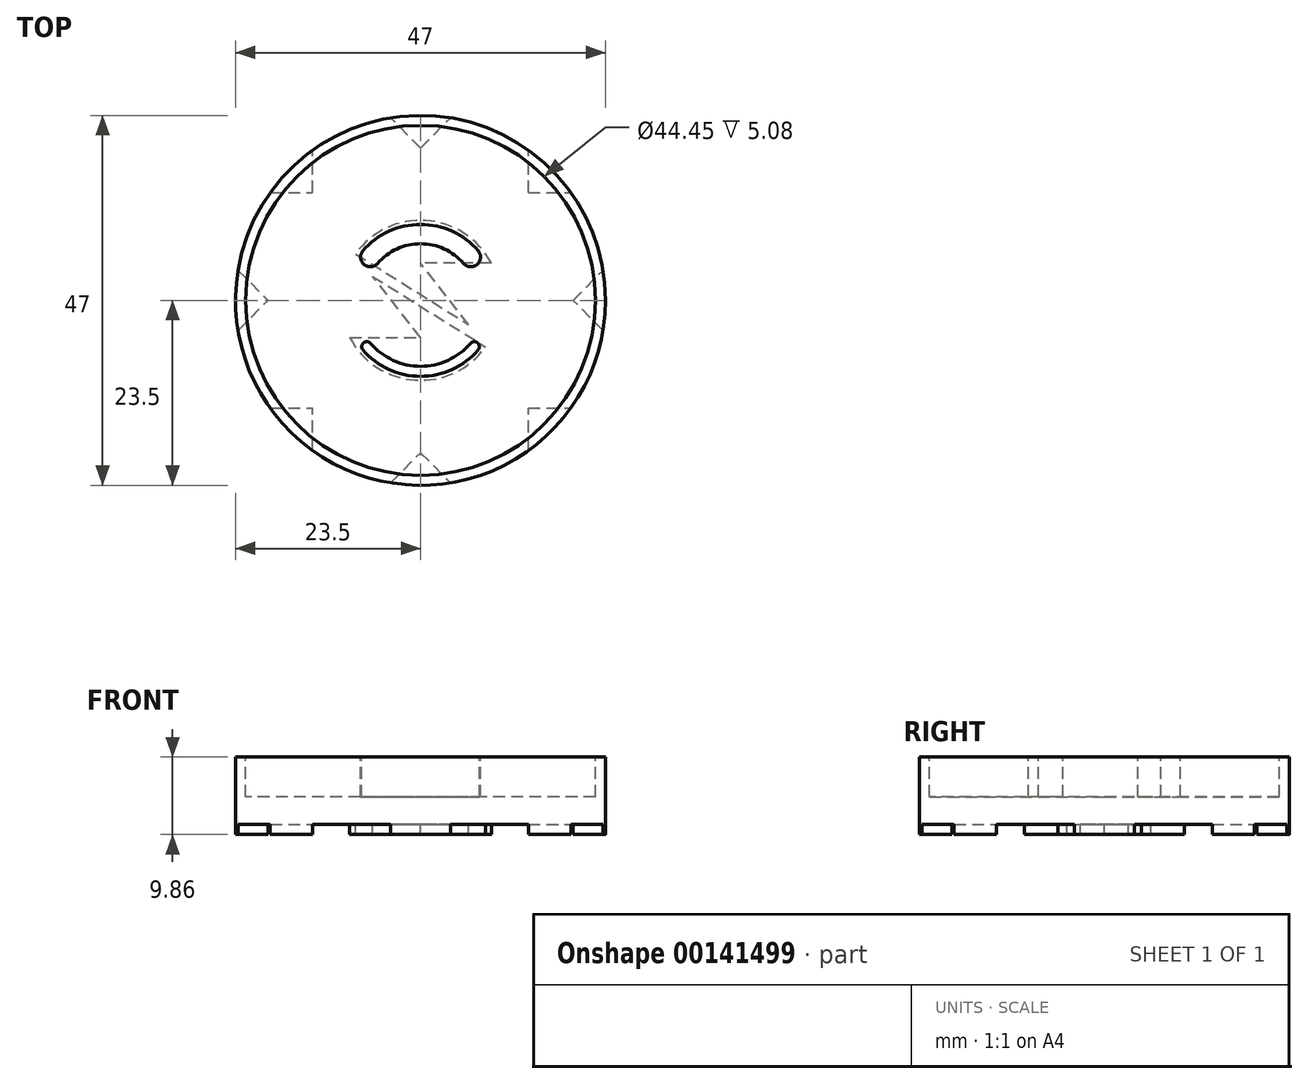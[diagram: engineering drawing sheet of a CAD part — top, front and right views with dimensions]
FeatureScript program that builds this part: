
annotation { "Feature Type Name" : "Feature", "Feature Type Description" : "" }
export const myFeature = defineFeature(function(context is Context, id is Id, definition is map)
    precondition{}
    {
        {
            var Q0;
            Q0=qCreatedBy(makeId("Top.planeOp"),FACE);
            var sketch = newSketch(context, id + "F0", { "sketchPlane" : qUnion([Q0])});
            skCircle(sketch, "E0", {"center": v(0, 0) * mm, "radius": 23.5 * mm});
            skSolve(sketch);
        }
        {
            var Q0;
            Q0 = qSketchRegion(id + "F0", true);
            extrude(context, id + "F1", {"entities" : qUnion([Q0]), "depth" : 8.6 * mm});
        }
        {
            var Q0;
            Q0=makeQuery(id+"F1.opExtrude","CAP_FACE",FACE,{"disambiguationData":[OSD([sQuery(id+"F0.wireOp",EDGE,"E0")])],"isStart":false});
            var sketch = newSketch(context, id + "F2", { "sketchPlane" : qUnion([Q0])});
            skCircle(sketch, "E1", {"center": v(0, 0) * mm, "radius": 22.23 * mm});
            skArc(sketch, "E2", {"start": v(-7.31, -6.3) * mm, "mid": v(0, -9.65) * mm, "end": v(7.31, -6.3) * mm});
            skArc(sketch, "E3", {"start": v(5.45, 4.7) * mm, "mid": v(0, 7.19) * mm, "end": v(-5.45, 4.7) * mm});
            skArc(sketch, "E4", {"start": v(-6.35, -5.47) * mm, "mid": v(0, -8.38) * mm, "end": v(6.35, -5.47) * mm});
            skArc(sketch, "E5", {"start": v(-7.31, 6.3) * mm, "mid": v(-7.18, 4.56) * mm, "end": v(-5.45, 4.7) * mm});
            skArc(sketch, "E6", {"start": v(5.45, 4.7) * mm, "mid": v(7.18, 4.56) * mm, "end": v(7.31, 6.3) * mm});
            skLineSegment(sketch, "E7", {"start": v(0, 0) * mm, "end": v(-7.31, 6.3) * mm, "construction": true});
            skLineSegment(sketch, "E8", {"start": v(0, 0) * mm, "end": v(7.31, 6.3) * mm, "construction": true});
            skArc(sketch, "E9", {"start": v(-6.35, -5.47) * mm, "mid": v(-7.25, -5.4) * mm, "end": v(-7.31, -6.3) * mm});
            skArc(sketch, "E10", {"start": v(7.31, -6.3) * mm, "mid": v(7.25, -5.4) * mm, "end": v(6.35, -5.47) * mm});
            skLineSegment(sketch, "E11", {"start": v(0, 0) * mm, "end": v(-7.31, -6.3) * mm, "construction": true});
            skLineSegment(sketch, "E12", {"start": v(0, 0) * mm, "end": v(7.31, -6.3) * mm, "construction": true});
            skArc(sketch, "E13.trimOffspring", {"start": v(7.31, 6.3) * mm, "mid": v(0, 9.65) * mm, "end": v(-7.31, 6.3) * mm});
            skSolve(sketch);
        }
        {
            var Q0;
            Q0=makeQuery(id+"F2.imprint","IMPRINT",FACE,{"disambiguationData":[TD([[makeQuery(id+"F2.imprint","IMPRINT",EDGE,{"derivedFrom":sQuery(id+"F2.wireOp",EDGE,"E1")}),1.0]])]});
            extrude(context, id + "F3", {"entities" : qUnion([Q0]), "operationType" : NewBodyOperationType.REMOVE, "oppositeDirection" : true, "depth" : 5.08 * mm});
        }
        {
            var Q0;
            Q0=makeQuery(id+"F1.opExtrude","CAP_FACE",FACE,{"disambiguationData":[OSD([sQuery(id+"F0.wireOp",EDGE,"E0")])],"isStart":true});
            var sketch = newSketch(context, id + "F4", { "sketchPlane" : qUnion([Q0])});
            skLineSegment(sketch, "E14", {"start": v(-3.81, 23.18) * mm, "end": v(0, 19.37) * mm});
            skLineSegment(sketch, "E15", {"start": v(-23.18, -3.81) * mm, "end": v(-19.37, 0) * mm});
            skLineSegment(sketch, "E16", {"start": v(-19.09, 13.7) * mm, "end": v(-13.7, 13.7) * mm});
            skLineSegment(sketch, "E17", {"start": v(13.7, 19.09) * mm, "end": v(13.7, 13.7) * mm});
            skLineSegment(sketch, "E18", {"start": v(-13.7, 19.09) * mm, "end": v(-13.7, 13.7) * mm});
            skLineSegment(sketch, "E19", {"start": v(-23.18, 3.81) * mm, "end": v(-19.37, 0) * mm});
            skLineSegment(sketch, "E20", {"start": v(16.61, 16.61) * mm, "end": v(-16.61, -16.61) * mm, "construction": true});
            skLineSegment(sketch, "E21", {"start": v(-19.09, -13.7) * mm, "end": v(-13.7, -13.7) * mm});
            skLineSegment(sketch, "E22", {"start": v(23.18, 3.81) * mm, "end": v(19.37, 0) * mm});
            skLineSegment(sketch, "E23.trimOffspring", {"start": v(13.7, 13.7) * mm, "end": v(19.09, 13.7) * mm});
            skLineSegment(sketch, "E24.trimOffspring", {"start": v(-13.7, -13.7) * mm, "end": v(-13.7, -19.09) * mm});
            skLineSegment(sketch, "E25.trimOffspring", {"start": v(0, 19.37) * mm, "end": v(3.81, 23.18) * mm});
            skLineSegment(sketch, "E26.trimOffspring", {"start": v(0, -19.37) * mm, "end": v(3.81, -23.18) * mm});
            skLineSegment(sketch, "E27.trimOffspring", {"start": v(13.7, -13.7) * mm, "end": v(19.09, -13.7) * mm});
            skLineSegment(sketch, "E28.trimOffspring", {"start": v(0, -19.37) * mm, "end": v(-3.81, -23.18) * mm});
            skLineSegment(sketch, "E29.trimOffspring", {"start": v(19.37, 0) * mm, "end": v(23.18, -3.81) * mm});
            skLineSegment(sketch, "E30.trimOffspring", {"start": v(13.7, -13.7) * mm, "end": v(13.7, -19.09) * mm});
            skSolve(sketch);
        }
        {
            var Q0;
            {var subQ0=sQuery(id+"F4.wireOp",EDGE,"E21");Q0=makeQuery(id+"F4.imprint","IMPRINT",FACE,{"disambiguationData":[TD([[makeQuery(id+"F4.imprint","IMPRINT",EDGE,{"derivedFrom":subQ0}),-1.0]])]});}
            var Q1;
            {var subQ0=sQuery(id+"F4.wireOp",EDGE,"E15");Q1=makeQuery(id+"F4.imprint","IMPRINT",FACE,{"disambiguationData":[TD([[makeQuery(id+"F4.imprint","IMPRINT",EDGE,{"derivedFrom":subQ0}),1.0]])]});}
            var Q2;
            {var subQ0=sQuery(id+"F4.wireOp",EDGE,"E16");Q2=makeQuery(id+"F4.imprint","IMPRINT",FACE,{"disambiguationData":[TD([[makeQuery(id+"F4.imprint","IMPRINT",EDGE,{"derivedFrom":subQ0}),1.0]])]});}
            var Q3;
            {var subQ0=sQuery(id+"F4.wireOp",EDGE,"E14");Q3=makeQuery(id+"F4.imprint","IMPRINT",FACE,{"disambiguationData":[TD([[makeQuery(id+"F4.imprint","IMPRINT",EDGE,{"derivedFrom":subQ0}),1.0]])]});}
            var Q4;
            {var subQ0=sQuery(id+"F4.wireOp",EDGE,"E17");Q4=makeQuery(id+"F4.imprint","IMPRINT",FACE,{"disambiguationData":[TD([[makeQuery(id+"F4.imprint","IMPRINT",EDGE,{"derivedFrom":subQ0}),1.0]])]});}
            var Q5;
            {var subQ0=sQuery(id+"F4.wireOp",EDGE,"E22");Q5=makeQuery(id+"F4.imprint","IMPRINT",FACE,{"disambiguationData":[TD([[makeQuery(id+"F4.imprint","IMPRINT",EDGE,{"derivedFrom":subQ0}),1.0]])]});}
            var Q6;
            {var subQ0=sQuery(id+"F4.wireOp",EDGE,"E27.trimOffspring");Q6=makeQuery(id+"F4.imprint","IMPRINT",FACE,{"disambiguationData":[TD([[makeQuery(id+"F4.imprint","IMPRINT",EDGE,{"derivedFrom":subQ0}),-1.0]])]});}
            var Q7;
            {var subQ0=sQuery(id+"F4.wireOp",EDGE,"E26.trimOffspring");Q7=makeQuery(id+"F4.imprint","IMPRINT",FACE,{"disambiguationData":[TD([[makeQuery(id+"F4.imprint","IMPRINT",EDGE,{"derivedFrom":subQ0}),-1.0]])]});}
            extrude(context, id + "F5", {"entities" : qUnion([Q0, Q1, Q2, Q3, Q4, Q5, Q6, Q7]), "operationType" : NewBodyOperationType.ADD, "depth" : 1.27 * mm});
        }
        {
            var Q0;
            Q0=makeQuery(id+"F1.opExtrude","CAP_FACE",FACE,{"disambiguationData":[OSD([sQuery(id+"F0.wireOp",EDGE,"E0")])],"isStart":true});
            var sketch = newSketch(context, id + "F6", { "sketchPlane" : qUnion([Q0])});
            skArc(sketch, "E31", {"start": v(-8.26, -5.91) * mm, "mid": v(0.7, -10.14) * mm, "end": v(9, -4.73) * mm});
            skLineSegment(sketch, "E32", {"start": v(0, 4.73) * mm, "end": v(-6.08, -3.05) * mm});
            skLineSegment(sketch, "E33", {"start": v(-9, 4.73) * mm, "end": v(0, 4.73) * mm});
            skLineSegment(sketch, "E34", {"start": v(9, -4.73) * mm, "end": v(0, -4.73) * mm});
            skLineSegment(sketch, "E35", {"start": v(-6.08, -3.05) * mm, "end": v(8.26, 5.91) * mm});
            skLineSegment(sketch, "E36", {"start": v(-8.26, -5.91) * mm, "end": v(6.08, 3.05) * mm});
            skLineSegment(sketch, "E37", {"start": v(6.08, 3.05) * mm, "end": v(0, -4.73) * mm});
            skArc(sketch, "E38.trimOffspring", {"start": v(8.26, 5.91) * mm, "mid": v(-0.7, 10.14) * mm, "end": v(-9, 4.73) * mm});
            skSolve(sketch);
        }
        {
            var Q0;
            Q0=makeQuery(id+"F6.imprint","IMPRINT",FACE,{"disambiguationData":[TD([[makeQuery(id+"F6.imprint","IMPRINT",EDGE,{"derivedFrom":sQuery(id+"F6.wireOp",EDGE,"E31")}),1.0]])]});
            var Q1;
            Q1=makeQuery(id+"F6.imprint","IMPRINT",FACE,{"disambiguationData":[TD([[makeQuery(id+"F6.imprint","IMPRINT",EDGE,{"derivedFrom":sQuery(id+"F6.wireOp",EDGE,"E32")}),1.0]])]});
            extrude(context, id + "F7", {"entities" : qUnion([Q0, Q1]), "operationType" : NewBodyOperationType.ADD, "depth" : 1.27 * mm});
        }
    });
